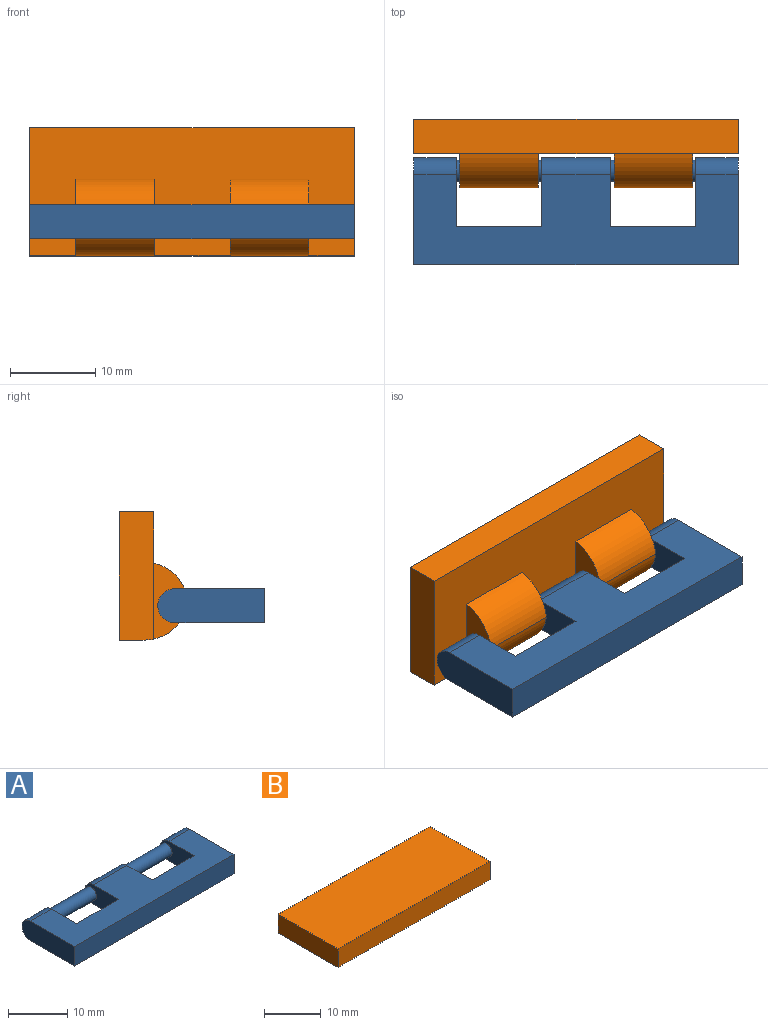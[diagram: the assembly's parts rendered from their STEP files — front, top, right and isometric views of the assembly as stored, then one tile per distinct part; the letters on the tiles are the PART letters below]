
ASSEMBLY  parts=2 mates=1
PART A: 16 faces, bbox 38x12.5x4 mm
  f0: plane 12.5x4mm, normal (-1,0,0), area 48.3mm2, adj f1,f5,f6,f15
  f1: plane 38x4mm, normal (0,-1,0), area 152mm2, adj f0,f5,f6,f7
  f2: plane 8x4mm, normal (-1,0,0), area 25.4mm2, adj f3,f5,f6,f12,f14
  f3: plane 10x4mm, normal (0,1,0), area 40mm2, adj f2,f4,f5,f6
  f4: plane 8x4mm, normal (1,0,0), area 25.4mm2, adj f3,f5,f6,f12,f15
  f5: plane 38x10.5mm, normal (0,0,1), area 279mm2, adj f0,f1,f2,f3,f4,f7,f8,f9
  f6: plane 38x10.5mm, normal (0,0,-1), area 279mm2, adj f0,f1,f2,f3,f4,f7,f8,f9
  f7: plane 12.5x4mm, normal (1,0,0), area 48.3mm2, adj f1,f5,f6,f13
  f8: plane 8x4mm, normal (1,0,0), area 25.4mm2, adj f5,f6,f9,f11,f14
  f9: plane 10x4mm, normal (0,1,0), area 40mm2, adj f5,f6,f8,f10
  f10: plane 8x4mm, normal (-1,0,0), area 25.4mm2, adj f5,f6,f9,f11,f13
  f11: cylinder r=1.25mm len=10mm, axis (-1,0,0), area 78.5mm2, adj f8,f10
  f12: cylinder r=1.25mm len=10mm, axis (-1,0,0), area 78.5mm2, adj f2,f4
  f13: cylinder r=2mm len=5mm, axis (-1,0,0), area 31.4mm2, adj f5,f6,f7,f10
  f14: cylinder r=2mm len=8mm, axis (1,0,0), area 50.3mm2, adj f2,f5,f6,f8
  f15: cylinder r=2mm len=5mm, axis (1,0,0), area 31.4mm2, adj f0,f4,f5,f6
PART B: 15 faces, bbox 38x15x8 mm
  f0: plane 38x3mm, normal (0,1,0), area 114mm2, adj f1,f3,f4,f13
  f1: plane 15x4mm, normal (-1,0,0), area 60mm2, adj f0,f2,f4,f5,f13
  f2: plane 38x4mm, normal (0,-1,0), area 152mm2, adj f1,f3,f4,f5
  f3: plane 15x4mm, normal (1,0,0), area 60mm2, adj f0,f2,f4,f5,f13
  f4: plane 38x15mm, normal (0,0,1), area 570mm2, adj f0,f1,f2,f3
  f5: plane 38x14.9mm, normal (0,0,-1), area 402.4mm2, adj f1,f2,f3,f6,f7,f8,f9,f12
  f6: plane 8.9x3.98mm, normal (-1,0,0), area 19.6mm2, adj f5,f11,f12,f13
  f7: plane 8.9x3.98mm, normal (1,0,0), area 19.6mm2, adj f5,f11,f12,f13
  f8: plane 8.9x3.98mm, normal (-1,0,0), area 19.6mm2, adj f5,f10,f13,f14
  f9: plane 8.9x3.98mm, normal (1,0,0), area 19.6mm2, adj f5,f10,f13,f14
  f10: cylinder r=1.4mm len=9.2mm, axis (-1,0,0), area 80.9mm2, adj f8,f9
  f11: cylinder r=1.4mm len=9.2mm, axis (-1,0,0), area 80.9mm2, adj f6,f7
  f12: cylinder r=5mm len=9.2mm, axis (-1,0,0), area 58.9mm2, adj f5,f6,f7,f13
  f13: cylinder r=5mm len=38mm, axis (1,0,0), area 156mm2, adj f0,f1,f3,f5,f6,f7,f8,f9
  f14: cylinder r=5mm len=9.2mm, axis (-1,0,0), area 58.9mm2, adj f5,f8,f9,f13
PLACE A t=(-3.78,-5.88,3.71)mm fixed
PLACE B rot(axis=(-1,0,0),90deg) t=(-3.07,7.12,1.71)mm
MATE revolute B.f10 <-> A.f11  axis (-1,0,0) through (-12.78,5.12,5.71)mm
